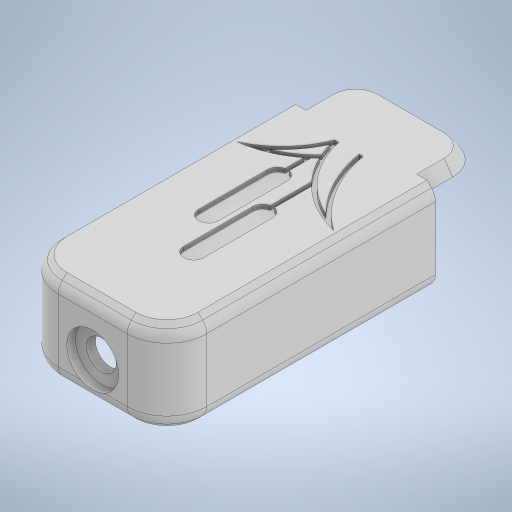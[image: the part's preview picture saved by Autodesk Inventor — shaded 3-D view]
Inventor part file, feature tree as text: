
AUTODESK INVENTOR PART (.ipt)
format: ipt  version: 2024 (Build 280153000, 153)  size: 686,080 bytes
history: native  units: in
note: dims shown in document units (in); Inventor stores cm internally (conversion verified against a paired STEP export)
features: extrude x11, sketch x7, move_body x5, fillet x3, direct_edit x3, sweep x2, chamfer x2
ambient origin geometry x8: Origin, YZ Plane, XZ Plane, XY Plane, X Axis, Y Axis, Z Axis, Center Point
bodies: Solid1 (feature_tree)
feature tree (33):
  extrude  "Extrusion1"  Depth=0.8465in
  extrude  "Extrusion2"  Depth=0.0689in
  fillet  "Fillet1"  Radius=0.1125in
  extrude  "Extrusion3"  Depth=0.1969in
  direct_edit  "Direct Edit1"
  sweep  "Sweep1"
  sweep  "Sweep2"
  extrude  "Extrusion11"  Depth=0.1181in
  extrude  "Extrusion12"  Depth=0.1181in
  extrude  "Extrusion13"  Depth=0.1181in
  chamfer  "Chamfer2"  [1 undecoded]
  fillet  "Fillet2"  Radius=0.6299in
  direct_edit  "Direct Edit2"
  extrude  "Extrusion14"  Depth=0.1181in
  chamfer  "Chamfer4"  Distance=0.0225in
  extrude  "Extrusion15"  Depth=0.703in
  fillet  "Fillet3"  Radius=0.5906in
  extrude  "Extrusion16"  Depth=0.1181in
  direct_edit  "Direct Edit3"
  extrude  "Extrusion17"  Depth=0.1181in
  extrude  "Extrusion18"  Depth=0.1181in
  sketch  "Sketch2"  dims[d0=1.9222in d1=0.8465in]
  sketch  "3D Sketch1"
  sketch  "3D Sketch2"
  sketch  "Sketch8"  dims[d2=0.0689in d3=0.0in d4=0.1969in d5=0.1125in]
  sketch  "Sketch11"  dims[d8=0.0225in d9=0.1969in d10=0.1125in d11=0.0225in]
  sketch  "Sketch12"  dims[d12=0.0281in d14=0.27in]
  sketch  "Sketch13"  dims[d16=0.2868in d17=0.0236in d18=0.0in d22=0.0225in d23=1.0124in d24=0.4499in d25=-0.225in d26=0.6299in d27=0.3543in d29=0.2812in d30=0.0225in d31=0.703in d32=0.5906in d33=0.5231in d34=0.5231in d36=0.0225in d37=0.0225in d39=0.4499in d40=0.0225in d41=0.0225in d42=0.0225in d43=0.0225in d44=0.0354in d45=1.0118in d46=0.27in d47=0.2812in d48=0.024in d49=0.126in d50=-0.0228in d51=0.1169in d52=0.045in d53=0.045in d54=-0.2811in d57=0.2264in d61=0.1004in d62=0.3858in d63=0.0in d64=0.5217in d65=0.6299in d66=0.1181in d68=0.3484in d69=1.8799in d70=0.315in d71=1.1029in d87=0.0in d88=0.0in d89=0.0689in d90=0.3779in d91=0.0689in d92=0.0in d93=0.0in d94=0.0in d95=0.0in d96=0.1457in d97=0.2953in d98=0.1693in d103=0.0846in d104=0.0846in d105=0.3937in d106=0.0in d107=0.3937in d108=0.0in d109=0.0492in d110=0.0in d111=0.0492in d112=0.0787in d113=45.0deg d114=0.0787in d115=0.2264in d116=1.0482in d117=1.0482in d118=0.689in d119=1.0482in d120=0.3445in d121=1.0482in d122=0.0in d123=1.8701in d124=1.8701in d129=0.0in d130=0.0in d131=-0.0059in d132=0.0in d133=0.0in d134=-0.0059in d135=0.0in d136=0.0in d137=-0.0059in d139=0.5236in d140=0.1201in d141=0.0in d142=0.0197in d143=0.0787in d144=45.0deg d145=0.041in d147=0.2756in d148=0.315in d149=0.189in d150=0.0in d151=0.0984in d153=0.2559in d154=0.0in d155=0.0in d156=0.0in d157=0.4838in d158=0.3543in d159=0.1201in d160=0.0in d161=0.1181in d162=0.0in d163=0.0in d164=0.1004in d165=1.0647in d169=0.0709in d170=0.1358in d166=0.0197in d167=0.0344in]
  move_body  "Move1"
  move_body  "Move2"
  move_body  "Move3"
  move_body  "Move4"
  move_body  "Move5"
note: 1 required parameter value undecoded (feature->parameter linkage not recoverable at this tier; creation-order binding heuristic only, values carry confidence <= 0.55)
